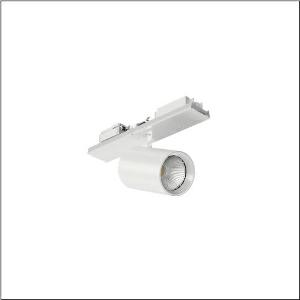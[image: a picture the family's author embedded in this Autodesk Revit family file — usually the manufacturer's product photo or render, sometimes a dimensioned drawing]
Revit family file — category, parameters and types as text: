
# Revit family: licross_r__spot_31_51sl127a45b_74df
name_source: partatom
category: Lighting Fixtures
units: mm (PartAtom-declared; Revit-internal decimal feet)

## family parameters
Cut with Voids When Loaded = No
Host = Face
Light Source = No
Part Type = Normal
Room Calculation Point = No
Round Connector Dimension = Use Diameter
Shared = No

## types (1)
- --- (1 x LED, 5140 lm, 42.6 W, 4000K)
    Apparent Load = 43 VA
    CIE Flux Codes = 93 97 99 100 100
    Color Rendering = 90
    Color Temperature = 4000K
    Default Elevation = 1800 mm
    Description = Licross® Spot 31, directional spotlight, light control with lens, of plastic, LED rated luminous flux: 5.140lm, light colour: 940, with plug, 3-pole, with phase selection, mains connection: 220..240V, AC, 50/60Hz, of aluminium, traffic white (RAL 9016), length: 140mm, diameter: 90mm, protection rating (complete): IP20, insulation class (complete): insulation class I (protective earthing), certification: CE, packaging unit: 1 piece
    Height = 175 mm
    Lamp = 1 x LED
    Lamp Light Flux = 5140 lm
    Lamp Power = 42.6 W
    Lamp count = 1
    Length = 90 mm
    Luminous efficacy = 121 lm/W
    Manufacturer = Siteco
    ModVariant = No
    Model = 51SL127A45B
    Mounting Place = Ceiling
    Mounting Type = Pendant
    Number of Poles = 1
    OnlyDefault = Yes
    Power Factor = 1
    Product Name = Licross® Spot 31
    Product group = directional spotlight
    ProductGroupID = 905
    Protection Class = Protection class I
    Protection Degree = IP 20
    RLX_Detail_Level = 1
    RLX_Emergency_Light_Flux = 0 lm
    RLX_Emergency_Type = 0
    RLX_Emergency_Type_DB = No
    RlxData = <blob elided: 14797 chars, md5=32ad13e9>
    Socket = socket
    Standby Power = 0 W
    System Light Flux = 5140 lm
    System Power = 43 W
    Type Comments = factory setting: luminous flux: 100 % | (ON | ON | ON) | 1050 mA
    Type Image = l_1245720.jpg
    URL = http://relux.com
    VarID = @adj_082115
    Voltage = 0 V
    Weight = 0.00 kg
    Width = 0 mm  [stored 0 ft]

note: [stored X ft] marks values corroborated as IEEE doubles in the binary element streams (Revit-internal decimal feet)

## geometry (parser evidence)
native form markers: Sweep x13
no freeform markers — native parametric forms only
